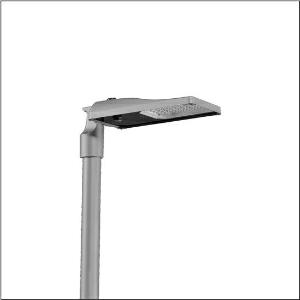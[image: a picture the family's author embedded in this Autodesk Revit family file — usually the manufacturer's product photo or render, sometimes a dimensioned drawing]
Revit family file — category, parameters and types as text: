
# Revit family: streetlight_sl_31_mini___stw1_0a_5xh6e31t08ja_04bd
name_source: partatom
category: Lighting Fixtures
units: mm (PartAtom-declared; Revit-internal decimal feet)

## family parameters
Cut with Voids When Loaded = No
Host = Face
Light Source = No
Part Type = Normal
Room Calculation Point = No
Round Connector Dimension = Use Diameter
Shared = No

## types (1)
- --- (1 x LED, 12270 lm, 82.5 W, 3000K)
    Apparent Load = 83 VA
    CIE Flux Codes = 39 75 98 100 100
    Color Rendering = 70
    Color Temperature = 3000K
    Default Elevation = 1800 mm
    Description = Streetlight SL 31 mini, mast luminaire, primary light control with lens, of PMMA, primary optical cover: cover, of toughened safety glass, transparent, light distribution: STW1.0a, light emission: direct distribution, primary light characteristic: asymmetric, installation type: post-top, side-entry, LED, High Power LED, rated luminous flux: 12.270lm, luminous efficacy: 149lm/W, light colour: 730, colour temperature: 3000K, control: presetting dimming logarithmic, flexible luminous flux parameterisation, time-dependent luminous flux control, constant luminous flux control, power reduction, intelligent temperature release in ECG and LED module, overheat protection, with cable H07RN-F 2x 1.5mm², mains connection: 220..240V, AC, 50/60Hz, connection cable pre-assembled, cable length: 10,5m, start of lifetime: 83W, end of service life: 90W, reduction: 37W, luminaire housing, of diecast aluminium, powder-coated, Siteco® metallic grey (DB 702S), corrosivity category C5 high according to DIN EN ISO 12944, sealing non-destructively replaceable, multi-level sealing system, mast flange (76/60mm) included as standard, inclination: -15°..+20° (post-top) | -20°..+20° (side-entry), adjustable in 5° steps, no sealing on luminaire upper side, Smart Interface below and above, protection rating (complete): IP66, insulation class (complete): insulation class II (safety insulation), certification: CE, ENEC, ENEC+, VDE, UKCA, ZD4i, impact resistance: IK09, permissible operating ambient temperature for outdoor applications: -40..+50°C, standard-compliant lighting for roads and squares, packaging unit: 1 piece

Light Distribution: STW1.0a
    Height = 76 mm
    Lamp = 1 x LED
    Lamp Light Flux = 12270 lm
    Lamp Power = 82.5 W
    Lamp count = 1
    Length = 547 mm
    Luminous efficacy = 149 lm/W
    Manufacturer = Siteco
    ModVariant = No
    Model = 5XH6E31T08JA
    Number of Poles = 1
    OnlyDefault = Yes
    Power Factor = 1
    Product Name = Streetlight SL 31 mini | STW1.0a
    Product group = mast luminaire | pylon top
    ProductGroupID = 6100
    Protection Class = Protection class II
    Protection Degree = IP 66
    RLX_Detail_Level = 1
    RLX_Emergency_Light_Flux = 0 lm
    RLX_Emergency_Type = 0
    RLX_Emergency_Type_DB = No
    RlxData = <blob elided: 40297 chars, md5=1ffcf8cc>
    Socket = socket
    Standby Power = 0 W
    System Light Flux = 12270 lm
    System Power = 83 W
    Type Comments = factory setting: luminous flux: 100 % | dim-lin: 254 | 870 mA
    Type Image = l_1300332.jpg
    URL = http://relux.com
    VarID = @adj_007455
    Voltage = 0 V
    Weight = 0.00 kg
    Width = 265 mm

## geometry (parser evidence)
native form markers: Blend x4, Sweep x11
no freeform markers — native parametric forms only
